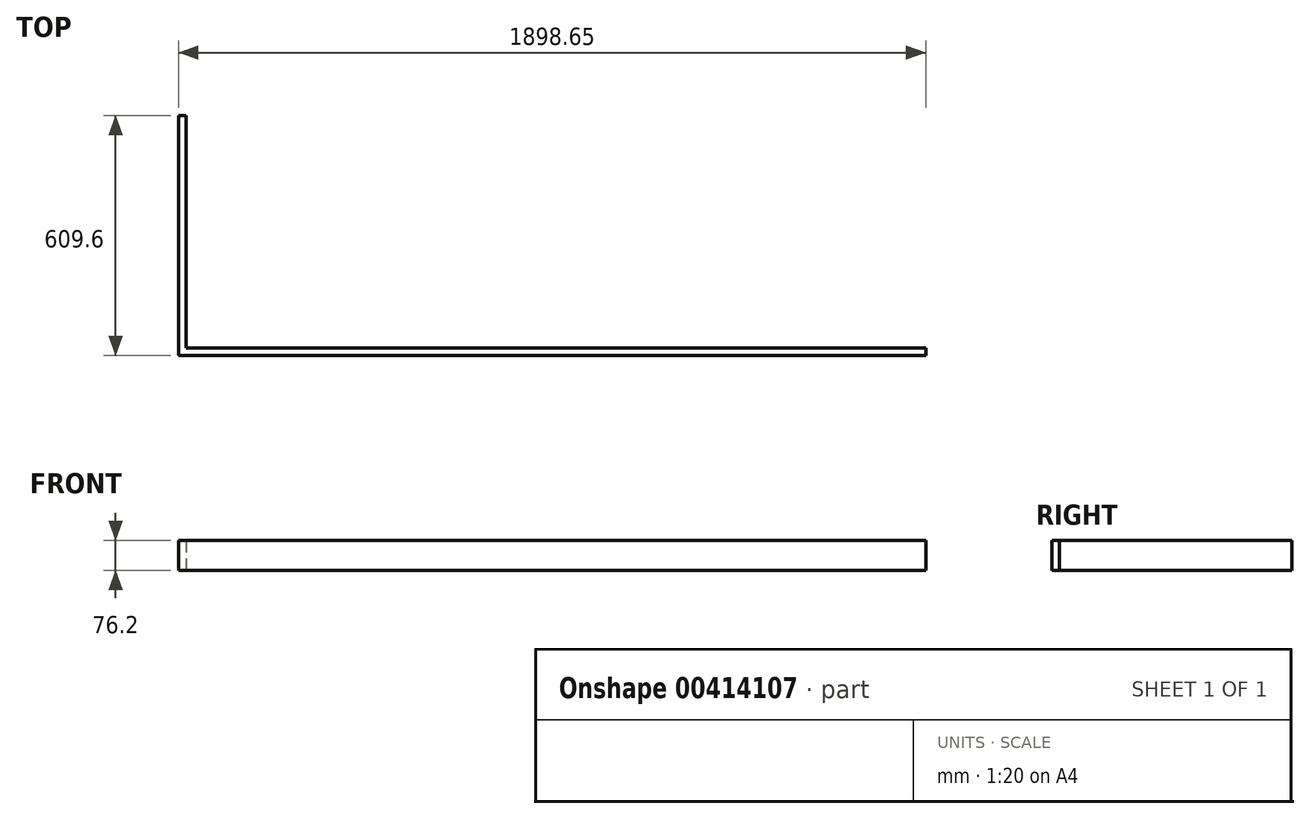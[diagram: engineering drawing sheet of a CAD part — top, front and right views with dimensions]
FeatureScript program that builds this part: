
annotation { "Feature Type Name" : "Feature", "Feature Type Description" : "" }
export const myFeature = defineFeature(function(context is Context, id is Id, definition is map)
    precondition{}
    {
        {
            var Q0;
            Q0=qCreatedBy(makeId("Top.planeOp"),FACE);
            var sketch = newSketch(context, id + "F0", { "sketchPlane" : qUnion([Q0])});
            skLineSegment(sketch, "E0", {"start": v(0, 0) * mm, "end": v(0, -590.55) * mm});
            skLineSegment(sketch, "E1", {"start": v(0, -590.55) * mm, "end": v(1879.6, -590.55) * mm});
            skSolve(sketch);
        }
        {
            var Q0;
            Q0=qCreatedBy(makeId("Front.planeOp"),FACE);
            var sketch = newSketch(context, id + "F1", { "sketchPlane" : qUnion([Q0])});
            skLineSegment(sketch, "E2", {"start": v(0, 0) * mm, "end": v(0, 76.2) * mm});
            skLineSegment(sketch, "E3", {"start": v(0, 76.2) * mm, "end": v(-19.05, 76.2) * mm});
            skLineSegment(sketch, "E4", {"start": v(-19.05, 76.2) * mm, "end": v(-19.05, 0) * mm});
            skLineSegment(sketch, "E5", {"start": v(-19.05, 0) * mm, "end": v(0, 0) * mm});
            skSolve(sketch);
        }
        {
            var Q0;
            Q0=makeQuery(id+"F1.imprint","IMPRINT",FACE,{"disambiguationData":[TD([[makeQuery(id+"F1.imprint","IMPRINT",EDGE,{"derivedFrom":sQuery(id+"F1.wireOp",EDGE,"E2")}),1.0]])]});
            var Q1;
            Q1=sQuery(id+"F0.wireOp",EDGE,"E0");
            var Q2;
            Q2=sQuery(id+"F0.wireOp",EDGE,"E1");
            sweep(context, id + "F2", {"profiles" : qUnion([Q0]), "path" : qUnion([Q1, Q2])});
        }
    });
